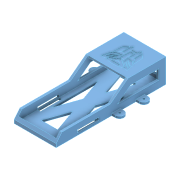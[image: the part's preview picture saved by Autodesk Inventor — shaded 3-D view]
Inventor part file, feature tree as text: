
AUTODESK INVENTOR PART (.ipt)
format: ipt  version: 2022 (Build 260153000, 153)  size: 470,528 bytes
history: native  units: mm
features: sketch x13, extrude x11, projected_geometry x10, fillet x2, rib x1, mirror x1, chamfer x1, hole x1
ambient origin geometry x8: Origin, YZ Plane, XZ Plane, XY Plane, X Axis, Y Axis, Z Axis, Center Point
bodies: Body1 (feature_tree)
feature tree (40):
  extrude  "Extrusion3"  Depth=51.0mm
  extrude  "Extrusion4"  Depth=3.0mm TaperAngle=0.0deg
  extrude  "Extrusion5"  Depth=3.0mm
  extrude  "Extrusion6"  Depth=5.0mm
  extrude  "Velcro Strap Hole"  Depth=3.0mm TaperAngle=0.0deg
  rib  "Rib1"
  mirror  "Mirror2"
  extrude  "Extrusion13"  Depth=5.0mm
  chamfer  "Chamfer4"  Distance=10.0mm
  extrude  "Extrusion8"  Depth=1.0mm
  extrude  "Extrusion9"  Depth=8.0mm TaperAngle=45.0deg
  hole  "Mounting Holes"  [1 undecoded]
  fillet  "Fillet1"  Radius=6.0mm
  extrude  "Extrusion10"  Depth=5.0mm
  extrude  "Autobots Logo"  Depth=30.0mm
  extrude  "Velcro Strap Hole 2"  Depth=34.0mm
  fillet  "Fillet2"  Radius=5.0mm
  sketch  "Sketch4"  dims[d25=51.0mm d26=143.0mm]
  sketch  "Sketch5"  dims[d27=4.0mm d28=3.0mm d29=0.0mm]
  sketch  "Sketch6"  dims[d30=3.0mm d31=3.0mm]
  sketch  "Sketch7"  dims[d33=50.0mm d34=0.0mm d36=5.0mm]
  sketch  "Sketch8"  dims[d37=3.0mm d38=3.0mm d39=0.0mm]
  sketch  "Sketch9"  dims[d40=15.0mm d41=5.0mm]
  sketch  "Sketch10"  dims[d42=0.0mm]
  sketch  "Sketch11"  dims[d43=30.0mm]
  sketch  "Sketch12"  dims[d45=4.0mm]
  sketch  "Sketch13"  dims[d46=45.0mm d47=10.0mm d48=0.0mm]
  sketch  "Sketch14"  dims[d49=25.0mm d50=1.0mm]
  sketch  "Sketch15"  dims[d51=3.0mm d52=0.0mm d53=0.0mm d54=1.0mm d55=1.0mm d56=8.0mm d57=10.0mm d58=45.0deg]
  sketch  "Sketch16"  dims[d59=10.0mm d60=10.0mm d61=0.0mm d62=6.0mm d64=5.0mm d65=30.0mm d66=34.0mm d67=5.0mm d68=6.0mm d69=10.0mm d70=0.0mm d71=3.4mm d72=6.0mm d73=4.0mm d74=2.0mm d75=90.0deg d76=6.0mm d77=0.0mm d78=5.0mm d81=20.0mm d82=10.0mm d83=15.0mm d84=10.0mm d85=0.0mm d86=1.0mm d87=0.0mm d88=28.0mm d89=3.0mm d90=3.0mm d91=10.0mm d92=0.0mm d93=3.0mm d94=3.0mm d95=10.0mm d96=0.0mm d97=1.0mm d99=0.5mm d100=0.872665mm d101=0.5mm d102=0.872665mm]
  projected_geometry  "Project Cut Edges2"
  projected_geometry  "Project Cut Edges3"
  projected_geometry  "Project Cut Edges4"
  projected_geometry  "Project Cut Edges5"
  projected_geometry  "Project Cut Edges6"
  projected_geometry  "Project Cut Edges7"
  projected_geometry  "Project Cut Edges8"
  projected_geometry  "Project Cut Edges9"
  projected_geometry  "Project Cut Edges10"
  projected_geometry  "Project Cut Edges11"
note: 1 required parameter value undecoded (feature->parameter linkage not recoverable at this tier; creation-order binding heuristic only, values carry confidence <= 0.55)
